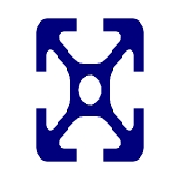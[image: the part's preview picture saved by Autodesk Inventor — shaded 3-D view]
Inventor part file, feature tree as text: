
AUTODESK INVENTOR PART (.ipt)
format: ipt  version: 2020 (Build 240168000, 168)  size: 273,408 bytes
history: native  units: mm
features: other x16, sketch x8
ambient origin geometry x8: Origin, YZ Plane, XZ Plane, XY Plane, X Axis, Y Axis, Z Axis, Center Point
bodies: Body (feature_tree)
feature tree (24):
  other  "Řízená délka"
  other  "Těleso1"
  other  "Start Plane"
  other  "End Plane"
  other  "iFeatureSketch"
  other  "DRAZKA_20:1"
  other  "DRAZKA_20:2"
  other  "DRAZKA_20:3"
  other  "DRAZKA_20:4"
  other  "DIRA_20:1"
  other  "DRAZKA_20:1Axis"
  other  "DRAZKA_20:2Axis"
  other  "DRAZKA_20:3Axis"
  other  "DRAZKA_20:4Axis"
  other  "DIRA_20:1Axis"
  sketch  "Sketch"  dims[d2=20.0mm d3=20.0mm d4=2.0mm d9=-0.0mm d10=400.0mm d11=0.13mm d12=0.0mm d15=0.83mm d16=0.83mm d17=9.8mm d18=3.0mm d19=4.55mm d20=45.0deg d21=5.2mm d22=1.8mm d24=1.0mm d26=0.83mm d27=0.83mm d28=9.8mm d29=3.0mm d30=4.55mm d31=45.0deg d32=5.2mm d33=1.8mm d35=1.0mm d37=0.83mm d38=0.83mm d39=9.8mm d40=3.0mm d41=4.55mm d42=45.0deg d43=5.2mm d44=1.8mm d46=1.0mm d48=0.83mm d49=0.83mm d50=9.8mm d51=3.0mm d52=4.55mm d53=45.0deg d54=5.2mm d55=1.8mm d57=1.0mm d59=4.3mm d60=0.0mm d61=0.0mm d62=0.0mm d63=0.0mm d64=0.0mm d65=0.0mm d66=0.0mm d67=0.0mm d76=90.0deg d14=400.0mm]
  sketch  "Náčrt11"
  other  "Pracovní rovina4"
  sketch  "Náčrt12"
  sketch  "Náčrt6"
  sketch  "Náčrt7"
  sketch  "Náčrt8"
  sketch  "Náčrt9"
  sketch  "Náčrt10"
